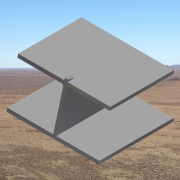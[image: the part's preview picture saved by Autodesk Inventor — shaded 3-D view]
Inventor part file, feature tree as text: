
AUTODESK INVENTOR PART (.ipt)
format: ipt  version: 2014 SP1 (Build 180222100, 222)  size: 165,376 bytes
history: native  units: in
note: dims shown in document units (in); Inventor stores cm internally (conversion verified against a paired STEP export)
features: sketch x4, other x3
ambient origin geometry x8: Origin, YZ Plane, XZ Plane, XY Plane, X Axis, Y Axis, Z Axis, Center Point
bodies: Solid1 (feature_tree)
feature tree (7):
  other  "endVert1.ipt"
  other  "Solid2::endVert1.ipt"
  other  "TaggingFeature1"
  sketch  "Sketch1"  dims[d0=0.3937in]
  sketch  "Sketch6"  dims[d2=0.12in d17=0.12in d18=3.0in d19=0.0in d20=15.0deg d21=-0.5in d22=1.0in d23=0.0in d24=0.05in d25=0.05in d26=0.005in d27=0.05in d28=0.17in d29=0.0in d30=0.0in d31=0.5in d32=0.0in]
  sketch  "Sketch7"
  sketch  "Sketch8"
